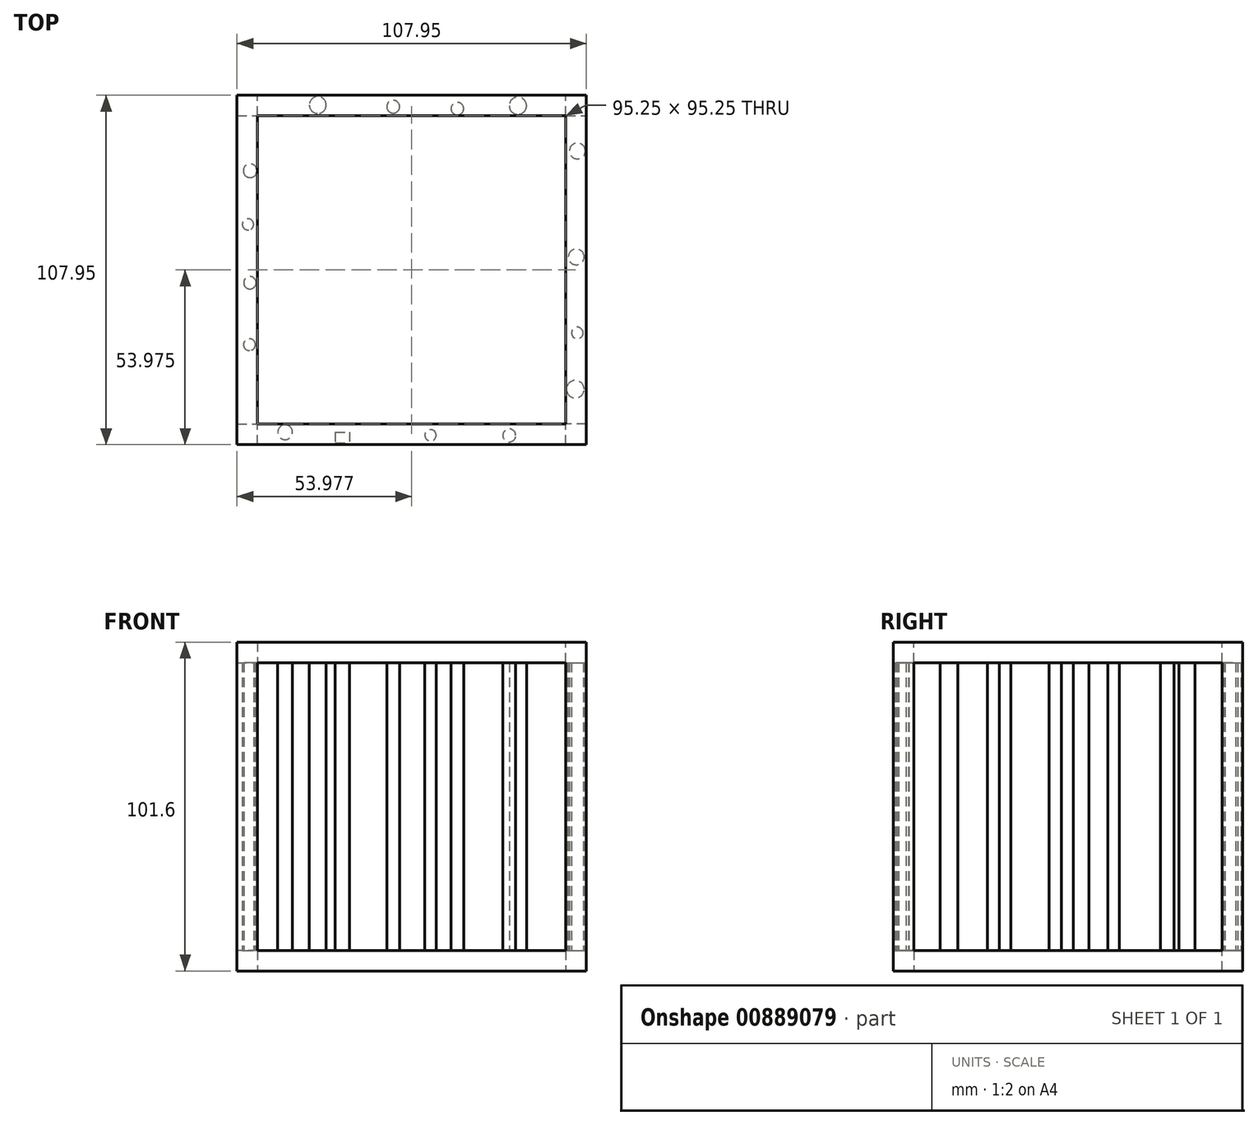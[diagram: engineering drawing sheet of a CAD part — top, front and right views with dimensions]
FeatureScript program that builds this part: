
annotation { "Feature Type Name" : "Feature", "Feature Type Description" : "" }
export const myFeature = defineFeature(function(context is Context, id is Id, definition is map)
    precondition{}
    {
        {
            var Q0;
            Q0=qCreatedBy(makeId("Top.planeOp"),FACE);
            var sketch = newSketch(context, id + "F0", { "sketchPlane" : qUnion([Q0])});
            skLineSegment(sketch, "E0.bottom", {"start": v(-52.32, 56.43) * mm, "end": v(-45.97, 56.43) * mm});
            skLineSegment(sketch, "E0.top", {"start": v(-52.32, 50.08) * mm, "end": v(-45.97, 50.08) * mm});
            skLineSegment(sketch, "E0.left", {"start": v(-52.32, 56.43) * mm, "end": v(-52.32, 50.08) * mm});
            skLineSegment(sketch, "E0.right", {"start": v(-45.97, 56.43) * mm, "end": v(-45.97, 50.08) * mm});
            skSolve(sketch);
        }
        {
            var Q0;
            Q0=makeQuery(id+"F0.imprint","IMPRINT",FACE,{"disambiguationData":[TD([[makeQuery(id+"F0.imprint","IMPRINT",EDGE,{"derivedFrom":sQuery(id+"F0.wireOp",EDGE,"E0.bottom")}),-1.0]])]});
            extrude(context, id + "F1", {"entities" : qUnion([Q0]), "depth" : 101.6 * mm, "offsetDistance" : 25.4 * mm});
        }
        {
            var Q0;
            Q0=makeQuery(id+"F1.opExtrude","SWEPT_FACE",FACE,{"disambiguationData":[OSD([sQuery(id+"F0.wireOp",EDGE,"E0.top")])]});
            var sketch = newSketch(context, id + "F2", { "sketchPlane" : qUnion([Q0])});
            skLineSegment(sketch, "E1.bottom", {"start": v(-45.97, 0) * mm, "end": v(-52.32, 0) * mm});
            skLineSegment(sketch, "E1.top", {"start": v(-45.97, 6.35) * mm, "end": v(-52.32, 6.35) * mm});
            skLineSegment(sketch, "E1.left", {"start": v(-45.97, 0) * mm, "end": v(-45.97, 6.35) * mm});
            skLineSegment(sketch, "E1.right", {"start": v(-52.32, 0) * mm, "end": v(-52.32, 6.35) * mm});
            skSolve(sketch);
        }
        {
            var Q0;
            Q0=makeQuery(id+"F2.imprint","IMPRINT",FACE,{"disambiguationData":[TD([[makeQuery(id+"F2.imprint","IMPRINT",EDGE,{"derivedFrom":sQuery(id+"F2.wireOp",EDGE,"E1.bottom")}),1.0]])]});
            extrude(context, id + "F3", {"entities" : qUnion([Q0]), "operationType" : NewBodyOperationType.ADD, "depth" : 101.6 * mm, "offsetDistance" : 25.4 * mm});
        }
        {
            var Q0;
            Q0=makeQuery(id+"F3.opExtrude","SWEPT_FACE",FACE,{"disambiguationData":[OSD([sQuery(id+"F2.wireOp",EDGE,"E1.top")])]});
            var sketch = newSketch(context, id + "F4", { "sketchPlane" : qUnion([Q0])});
            skLineSegment(sketch, "E2.bottom", {"start": v(-52.32, -51.52) * mm, "end": v(-45.97, -51.52) * mm});
            skLineSegment(sketch, "E2.top", {"start": v(-52.32, -45.17) * mm, "end": v(-45.97, -45.17) * mm});
            skLineSegment(sketch, "E2.left", {"start": v(-52.32, -51.52) * mm, "end": v(-52.32, -45.17) * mm});
            skLineSegment(sketch, "E2.right", {"start": v(-45.97, -51.52) * mm, "end": v(-45.97, -45.17) * mm});
            skSolve(sketch);
        }
        {
            var Q0;
            Q0=makeQuery(id+"F4.imprint","IMPRINT",FACE,{"disambiguationData":[TD([[makeQuery(id+"F4.imprint","IMPRINT",EDGE,{"derivedFrom":sQuery(id+"F4.wireOp",EDGE,"E2.bottom")}),-1.0]])]});
            extrude(context, id + "F5", {"entities" : qUnion([Q0]), "operationType" : NewBodyOperationType.ADD, "depth" : 95.25 * mm, "offsetDistance" : 25.4 * mm});
        }
        {
            var Q0;
            Q0=makeQuery(id+"F1.opExtrude","SWEPT_FACE",FACE,{"disambiguationData":[OSD([sQuery(id+"F0.wireOp",EDGE,"E0.top")])]});
            var sketch = newSketch(context, id + "F6", { "sketchPlane" : qUnion([Q0])});
            skLineSegment(sketch, "E3.bottom", {"start": v(-52.32, 101.6) * mm, "end": v(-45.97, 101.6) * mm});
            skLineSegment(sketch, "E3.top", {"start": v(-52.32, 95.25) * mm, "end": v(-45.97, 95.25) * mm});
            skLineSegment(sketch, "E3.left", {"start": v(-52.32, 101.6) * mm, "end": v(-52.32, 95.25) * mm});
            skLineSegment(sketch, "E3.right", {"start": v(-45.97, 101.6) * mm, "end": v(-45.97, 95.25) * mm});
            skSolve(sketch);
        }
        {
            var Q0;
            Q0 = qSketchRegion(id + "F6", true);
            extrude(context, id + "F7", {"entities" : qUnion([Q0]), "operationType" : NewBodyOperationType.ADD, "depth" : 99.82 * mm, "offsetDistance" : 25.4 * mm});
        }
        {
            var Q0;
            Q0=makeQuery(id+"F7.boolean.opBoolean","MERGE",FACE,{"derivedFrom":[makeQuery(id+"F5.boolean.opBoolean","MERGE",FACE,{"derivedFrom":[makeQuery(id+"F3.boolean.opBoolean","MERGE",FACE,{"derivedFrom":[makeQuery(id+"F1.opExtrude","SWEPT_FACE",FACE,{"disambiguationData":[OSD([sQuery(id+"F0.wireOp",EDGE,"E0.right")])]}),makeQuery(id+"F3.opExtrude","SWEPT_FACE",FACE,{"disambiguationData":[OSD([sQuery(id+"F2.wireOp",EDGE,"E1.left")])]})]}),makeQuery(id+"F5.opExtrude","SWEPT_FACE",FACE,{"disambiguationData":[OSD([sQuery(id+"F4.wireOp",EDGE,"E2.right")])]})]}),makeQuery(id+"F7.opExtrude","SWEPT_FACE",FACE,{"disambiguationData":[OSD([sQuery(id+"F6.wireOp",EDGE,"E3.right")])]})]});
            var sketch = newSketch(context, id + "F8", { "sketchPlane" : qUnion([Q0])});
            skLineSegment(sketch, "E4.bottom", {"start": v(56.43, 0) * mm, "end": v(50.08, 0) * mm});
            skLineSegment(sketch, "E4.top", {"start": v(56.43, 6.35) * mm, "end": v(50.08, 6.35) * mm});
            skLineSegment(sketch, "E4.left", {"start": v(56.43, 0) * mm, "end": v(56.43, 6.35) * mm});
            skLineSegment(sketch, "E4.right", {"start": v(50.08, 0) * mm, "end": v(50.08, 6.35) * mm});
            skSolve(sketch);
        }
        {
            var Q0;
            Q0=makeQuery(id+"F8.imprint","IMPRINT",FACE,{"disambiguationData":[TD([[makeQuery(id+"F8.imprint","IMPRINT",EDGE,{"derivedFrom":sQuery(id+"F8.wireOp",EDGE,"E4.bottom")}),-1.0]])]});
            extrude(context, id + "F9", {"entities" : qUnion([Q0]), "operationType" : NewBodyOperationType.ADD, "depth" : 101.6 * mm, "offsetDistance" : 25.4 * mm});
        }
        {
            var Q0;
            Q0=makeQuery(id+"F7.boolean.opBoolean","MERGE",FACE,{"derivedFrom":[makeQuery(id+"F5.boolean.opBoolean","MERGE",FACE,{"derivedFrom":[makeQuery(id+"F3.boolean.opBoolean","MERGE",FACE,{"derivedFrom":[makeQuery(id+"F1.opExtrude","SWEPT_FACE",FACE,{"disambiguationData":[OSD([sQuery(id+"F0.wireOp",EDGE,"E0.right")])]}),makeQuery(id+"F3.opExtrude","SWEPT_FACE",FACE,{"disambiguationData":[OSD([sQuery(id+"F2.wireOp",EDGE,"E1.left")])]})]}),makeQuery(id+"F5.opExtrude","SWEPT_FACE",FACE,{"disambiguationData":[OSD([sQuery(id+"F4.wireOp",EDGE,"E2.right")])]})]}),makeQuery(id+"F7.opExtrude","SWEPT_FACE",FACE,{"disambiguationData":[OSD([sQuery(id+"F6.wireOp",EDGE,"E3.right")])]})]});
            var sketch = newSketch(context, id + "F10", { "sketchPlane" : qUnion([Q0])});
            skLineSegment(sketch, "E5.bottom", {"start": v(-45.17, 6.35) * mm, "end": v(-51.52, 6.35) * mm});
            skLineSegment(sketch, "E5.top", {"start": v(-45.17, 0) * mm, "end": v(-51.52, 0) * mm});
            skLineSegment(sketch, "E5.left", {"start": v(-45.17, 6.35) * mm, "end": v(-45.17, 0) * mm});
            skLineSegment(sketch, "E5.right", {"start": v(-51.52, 6.35) * mm, "end": v(-51.52, 0) * mm});
            skSolve(sketch);
        }
        {
            var Q0;
            Q0 = qSketchRegion(id + "F10", true);
            var Q1;
            Q1=makeQuery(id+"F10.imprint","IMPRINT",FACE,{"disambiguationData":[TD([[makeQuery(id+"F10.imprint","IMPRINT",EDGE,{"derivedFrom":sQuery(id+"F10.wireOp",EDGE,"E5.bottom")}),1.0]])]});
            extrude(context, id + "F11", {"entities" : qUnion([Q0, Q1]), "operationType" : NewBodyOperationType.ADD, "depth" : 101.6 * mm, "offsetDistance" : 25.4 * mm});
        }
        {
            var Q0;
            Q0=makeQuery(id+"F9.opExtrude","SWEPT_FACE",FACE,{"disambiguationData":[OSD([sQuery(id+"F8.wireOp",EDGE,"E4.right")])]});
            var sketch = newSketch(context, id + "F12", { "sketchPlane" : qUnion([Q0])});
            skLineSegment(sketch, "E6.bottom", {"start": v(55.63, 6.35) * mm, "end": v(49.28, 6.35) * mm});
            skLineSegment(sketch, "E6.top", {"start": v(55.63, 0) * mm, "end": v(49.28, 0) * mm});
            skLineSegment(sketch, "E6.left", {"start": v(55.63, 6.35) * mm, "end": v(55.63, 0) * mm});
            skLineSegment(sketch, "E6.right", {"start": v(49.28, 6.35) * mm, "end": v(49.28, 0) * mm});
            skSolve(sketch);
        }
        {
            var Q0;
            Q0=makeQuery(id+"F12.imprint","IMPRINT",FACE,{"disambiguationData":[TD([[makeQuery(id+"F12.imprint","IMPRINT",EDGE,{"derivedFrom":sQuery(id+"F12.wireOp",EDGE,"E6.bottom")}),1.0]])]});
            extrude(context, id + "F13", {"entities" : qUnion([Q0]), "operationType" : NewBodyOperationType.ADD, "depth" : 97.54 * mm, "offsetDistance" : 25.4 * mm});
        }
        {
            var Q0;
            Q0=makeQuery(id+"F13.boolean.opBoolean","MERGE",FACE,{"derivedFrom":[makeQuery(id+"F9.opExtrude","SWEPT_FACE",FACE,{"disambiguationData":[OSD([sQuery(id+"F8.wireOp",EDGE,"E4.top")])]}),makeQuery(id+"F11.opExtrude","SWEPT_FACE",FACE,{"disambiguationData":[OSD([sQuery(id+"F10.wireOp",EDGE,"E5.bottom")])]}),makeQuery(id+"F13.opExtrude","SWEPT_FACE",FACE,{"disambiguationData":[OSD([sQuery(id+"F12.wireOp",EDGE,"E6.bottom")])]})]});
            var sketch = newSketch(context, id + "F14", { "sketchPlane" : qUnion([Q0])});
            skLineSegment(sketch, "E7.bottom", {"start": v(55.63, -51.52) * mm, "end": v(49.28, -51.52) * mm});
            skLineSegment(sketch, "E7.top", {"start": v(55.63, -45.17) * mm, "end": v(49.28, -45.17) * mm});
            skLineSegment(sketch, "E7.left", {"start": v(55.63, -51.52) * mm, "end": v(55.63, -45.17) * mm});
            skLineSegment(sketch, "E7.right", {"start": v(49.28, -51.52) * mm, "end": v(49.28, -45.17) * mm});
            skSolve(sketch);
        }
        {
            var Q0;
            Q0=makeQuery(id+"F14.imprint","IMPRINT",FACE,{"disambiguationData":[TD([[makeQuery(id+"F14.imprint","IMPRINT",EDGE,{"derivedFrom":sQuery(id+"F14.wireOp",EDGE,"E7.bottom")}),-1.0]])]});
            extrude(context, id + "F15", {"entities" : qUnion([Q0]), "operationType" : NewBodyOperationType.ADD, "depth" : 95.25 * mm, "offsetDistance" : 25.4 * mm});
        }
        {
            var Q0;
            Q0=makeQuery(id+"F15.opExtrude","SWEPT_FACE",FACE,{"disambiguationData":[OSD([sQuery(id+"F14.wireOp",EDGE,"E7.right")])]});
            var sketch = newSketch(context, id + "F16", { "sketchPlane" : qUnion([Q0])});
            skLineSegment(sketch, "E8.bottom", {"start": v(51.52, 101.6) * mm, "end": v(45.17, 101.6) * mm});
            skLineSegment(sketch, "E8.top", {"start": v(51.52, 95.25) * mm, "end": v(45.17, 95.25) * mm});
            skLineSegment(sketch, "E8.left", {"start": v(51.52, 101.6) * mm, "end": v(51.52, 95.25) * mm});
            skLineSegment(sketch, "E8.right", {"start": v(45.17, 101.6) * mm, "end": v(45.17, 95.25) * mm});
            skSolve(sketch);
        }
        {
            var Q0;
            Q0=makeQuery(id+"F16.imprint","IMPRINT",FACE,{"disambiguationData":[TD([[makeQuery(id+"F16.imprint","IMPRINT",EDGE,{"derivedFrom":sQuery(id+"F16.wireOp",EDGE,"E8.bottom")}),1.0]])]});
            extrude(context, id + "F17", {"entities" : qUnion([Q0]), "operationType" : NewBodyOperationType.ADD, "depth" : 96.52 * mm, "offsetDistance" : 25.4 * mm});
        }
        {
            var Q0;
            {var subQ2=sQuery(id+"F4.wireOp",EDGE,"E2.right");var subQ8=makeQuery(id+"F5.opExtrude","SWEPT_FACE",FACE,{"disambiguationData":[OSD([subQ2])]});var subQ9=sQuery(id+"F0.wireOp",EDGE,"E0.bottom");var subQ10=makeQuery(id+"F1.opExtrude","SWEPT_FACE",FACE,{"disambiguationData":[OSD([subQ9])]});var subQ12=sQuery(id+"F2.wireOp",EDGE,"E1.left");var subQ13=makeQuery(id+"F3.opExtrude","SWEPT_FACE",FACE,{"disambiguationData":[OSD([subQ12])]});var subQ14=sQuery(id+"F0.wireOp",EDGE,"E0.right");var subQ15=makeQuery(id+"F1.opExtrude","SWEPT_FACE",FACE,{"disambiguationData":[OSD([subQ14])]});var subQ22=makeQuery(id+"F7.opExtrude","SWEPT_FACE",FACE,{"disambiguationData":[OSD([sQuery(id+"F6.wireOp",EDGE,"E3.right")])]});Q0=makeQuery(id+"F17.boolean.opBoolean","SPLIT",FACE,{"disambiguationData":[TD([subQ10])],"derivedFrom":makeQuery(id+"F11.boolean.opBoolean","SPLIT",FACE,{"disambiguationData":[TD([subQ10])],"derivedFrom":makeQuery(id+"F7.boolean.opBoolean","MERGE",FACE,{"derivedFrom":[makeQuery(id+"F5.boolean.opBoolean","MERGE",FACE,{"derivedFrom":[makeQuery(id+"F3.boolean.opBoolean","MERGE",FACE,{"derivedFrom":[subQ15,subQ13]}),subQ8]}),subQ22]})})});}
            var sketch = newSketch(context, id + "F18", { "sketchPlane" : qUnion([Q0])});
            skLineSegment(sketch, "E9.bottom", {"start": v(50.08, 95.25) * mm, "end": v(56.43, 95.25) * mm});
            skLineSegment(sketch, "E9.top", {"start": v(50.08, 101.6) * mm, "end": v(56.43, 101.6) * mm});
            skLineSegment(sketch, "E9.left", {"start": v(50.08, 95.25) * mm, "end": v(50.08, 101.6) * mm});
            skLineSegment(sketch, "E9.right", {"start": v(56.43, 95.25) * mm, "end": v(56.43, 101.6) * mm});
            skSolve(sketch);
        }
        {
            var Q0;
            Q0=makeQuery(id+"F18.imprint","IMPRINT",FACE,{"disambiguationData":[TD([[makeQuery(id+"F18.imprint","IMPRINT",EDGE,{"derivedFrom":sQuery(id+"F18.wireOp",EDGE,"E9.bottom")}),1.0]])]});
            extrude(context, id + "F19", {"entities" : qUnion([Q0]), "operationType" : NewBodyOperationType.ADD, "depth" : 101.6 * mm, "offsetDistance" : 25.4 * mm});
        }
        {
            var Q0;
            Q0=makeQuery(id+"F19.opExtrude","SWEPT_FACE",FACE,{"disambiguationData":[OSD([sQuery(id+"F18.wireOp",EDGE,"E9.bottom")])]});
            var sketch = newSketch(context, id + "F20", { "sketchPlane" : qUnion([Q0])});
            skLineSegment(sketch, "E10.bottom", {"start": v(55.63, -50.08) * mm, "end": v(49.28, -50.08) * mm});
            skLineSegment(sketch, "E10.top", {"start": v(55.63, -56.43) * mm, "end": v(49.28, -56.43) * mm});
            skLineSegment(sketch, "E10.left", {"start": v(55.63, -50.08) * mm, "end": v(55.63, -56.43) * mm});
            skLineSegment(sketch, "E10.right", {"start": v(49.28, -50.08) * mm, "end": v(49.28, -56.43) * mm});
            skSolve(sketch);
        }
        {
            var Q0;
            Q0=makeQuery(id+"F20.imprint","IMPRINT",FACE,{"disambiguationData":[TD([[makeQuery(id+"F20.imprint","IMPRINT",EDGE,{"derivedFrom":sQuery(id+"F20.wireOp",EDGE,"E10.bottom")}),1.0]])]});
            extrude(context, id + "F21", {"entities" : qUnion([Q0]), "operationType" : NewBodyOperationType.ADD, "depth" : 92.2 * mm, "offsetDistance" : 25.4 * mm});
        }
        {
            var Q0;
            Q0=makeQuery(id+"F17.boolean.opBoolean","MERGE",FACE,{"derivedFrom":[makeQuery(id+"F15.opExtrude","SWEPT_FACE",FACE,{"disambiguationData":[OSD([sQuery(id+"F14.wireOp",EDGE,"E7.top")])]}),makeQuery(id+"F17.opExtrude","SWEPT_FACE",FACE,{"disambiguationData":[OSD([sQuery(id+"F16.wireOp",EDGE,"E8.right")])]})]});
            var sketch = newSketch(context, id + "F22", { "sketchPlane" : qUnion([Q0])});
            skLineSegment(sketch, "E11.bottom", {"start": v(-49.28, 95.25) * mm, "end": v(-55.63, 95.25) * mm});
            skLineSegment(sketch, "E11.top", {"start": v(-49.28, 101.6) * mm, "end": v(-55.63, 101.6) * mm});
            skLineSegment(sketch, "E11.left", {"start": v(-49.28, 95.25) * mm, "end": v(-49.28, 101.6) * mm});
            skLineSegment(sketch, "E11.right", {"start": v(-55.63, 95.25) * mm, "end": v(-55.63, 101.6) * mm});
            skSolve(sketch);
        }
        {
            var Q0;
            Q0 = qSketchRegion(id + "F22", true);
            extrude(context, id + "F23", {"entities" : qUnion([Q0]), "operationType" : NewBodyOperationType.ADD, "depth" : 97.28 * mm, "offsetDistance" : 25.4 * mm});
        }
        {
            var Q0;
            Q0=makeQuery(id+"F3.opExtrude","SWEPT_FACE",FACE,{"disambiguationData":[OSD([sQuery(id+"F2.wireOp",EDGE,"E1.top")])]});
            var sketch = newSketch(context, id + "F24", { "sketchPlane" : qUnion([Q0])});
            skCircle(sketch, "E12", {"center": v(-48.3, 33.1) * mm, "radius": 2.1 * mm});
            skSolve(sketch);
        }
        {
            var Q0;
            {var subQ1=makeQuery(id+"F13.opExtrude","SWEPT_FACE",FACE,{"disambiguationData":[OSD([sQuery(id+"F12.wireOp",EDGE,"E6.bottom")])]});var subQ2=sQuery(id+"F8.wireOp",EDGE,"E4.top");var subQ3=makeQuery(id+"F9.opExtrude","SWEPT_FACE",FACE,{"disambiguationData":[OSD([subQ2])]});var subQ4=sQuery(id+"F10.wireOp",EDGE,"E5.left");var subQ5=makeQuery(id+"F11.opExtrude","SWEPT_FACE",FACE,{"disambiguationData":[OSD([subQ4])]});var subQ7=sQuery(id+"F10.wireOp",EDGE,"E5.bottom");var subQ14=makeQuery(id+"F11.opExtrude","SWEPT_FACE",FACE,{"disambiguationData":[OSD([subQ7])]});Q0=makeQuery(id+"F21.boolean.opBoolean","SPLIT",FACE,{"disambiguationData":[TD([subQ5])],"derivedFrom":makeQuery(id+"F15.boolean.opBoolean","SPLIT",FACE,{"disambiguationData":[TD([makeQuery(id+"F1.opExtrude","SWEPT_FACE",FACE,{"disambiguationData":[OSD([sQuery(id+"F0.wireOp",EDGE,"E0.bottom")])]})])],"derivedFrom":makeQuery(id+"F13.boolean.opBoolean","MERGE",FACE,{"derivedFrom":[subQ3,subQ14,subQ1]})})});}
            var sketch = newSketch(context, id + "F25", { "sketchPlane" : qUnion([Q0])});
            skCircle(sketch, "E13", {"center": v(52.84, 39.23) * mm, "radius": 2.46 * mm});
            skSolve(sketch);
        }
        {
            var Q0;
            Q0=makeQuery(id+"F25.imprint","IMPRINT",FACE,{"disambiguationData":[TD([[makeQuery(id+"F25.imprint","IMPRINT",EDGE,{"derivedFrom":sQuery(id+"F25.wireOp",EDGE,"E13")}),-1.0]])]});
            var sketch = newSketch(context, id + "F26", { "sketchPlane" : qUnion([Q0])});
            skCircle(sketch, "E14", {"center": v(52.49, 6.48) * mm, "radius": 2.45 * mm});
            skSolve(sketch);
        }
        {
            var Q0;
            Q0=makeQuery(id+"F26.imprint","IMPRINT",FACE,{"disambiguationData":[TD([[makeQuery(id+"F26.imprint","IMPRINT",EDGE,{"derivedFrom":sQuery(id+"F26.wireOp",EDGE,"E14")}),-1.0]])]});
            var sketch = newSketch(context, id + "F27", { "sketchPlane" : qUnion([Q0])});
            skCircle(sketch, "E15", {"center": v(52.83, -17) * mm, "radius": 1.8 * mm});
            skSolve(sketch);
        }
        {
            var Q0;
            Q0=makeQuery(id+"F25.imprint","IMPRINT",FACE,{"disambiguationData":[TD([[makeQuery(id+"F25.imprint","IMPRINT",EDGE,{"derivedFrom":sQuery(id+"F25.wireOp",EDGE,"E13")}),1.0]])]});
            extrude(context, id + "F28", {"entities" : qUnion([Q0]), "operationType" : NewBodyOperationType.ADD, "depth" : 89.92 * mm, "offsetDistance" : 25.4 * mm});
        }
        {
            var Q0;
            Q0=makeQuery(id+"F26.imprint","IMPRINT",FACE,{"disambiguationData":[TD([[makeQuery(id+"F26.imprint","IMPRINT",EDGE,{"derivedFrom":sQuery(id+"F26.wireOp",EDGE,"E14")}),1.0]])]});
            extrude(context, id + "F29", {"entities" : qUnion([Q0]), "operationType" : NewBodyOperationType.ADD, "depth" : 91.19 * mm, "offsetDistance" : 25.4 * mm});
        }
        {
            var Q0;
            Q0=makeQuery(id+"F27.imprint","IMPRINT",FACE,{"disambiguationData":[TD([[makeQuery(id+"F27.imprint","IMPRINT",EDGE,{"derivedFrom":sQuery(id+"F27.wireOp",EDGE,"E15")}),-1.0]])]});
            var sketch = newSketch(context, id + "F30", { "sketchPlane" : qUnion([Q0])});
            skCircle(sketch, "E16", {"center": v(52.2, -34.4) * mm, "radius": 2.72 * mm});
            skSolve(sketch);
        }
        {
            var Q0;
            Q0 = qSketchRegion(id + "F30", true);
            extrude(context, id + "F31", {"entities" : qUnion([Q0]), "operationType" : NewBodyOperationType.ADD, "depth" : 91.19 * mm, "offsetDistance" : 25.4 * mm});
        }
        {
            var Q0;
            Q0=makeQuery(id+"F27.imprint","IMPRINT",FACE,{"disambiguationData":[TD([[makeQuery(id+"F27.imprint","IMPRINT",EDGE,{"derivedFrom":sQuery(id+"F27.wireOp",EDGE,"E15")}),1.0]])]});
            extrude(context, id + "F32", {"entities" : qUnion([Q0]), "operationType" : NewBodyOperationType.ADD, "depth" : 92.46 * mm, "offsetDistance" : 25.4 * mm});
        }
        {
            var Q0;
            {var subQ0=makeQuery(id+"F11.opExtrude","SWEPT_FACE",FACE,{"disambiguationData":[OSD([sQuery(id+"F10.wireOp",EDGE,"E5.bottom")])]});var subQ1=makeQuery(id+"F9.opExtrude","SWEPT_FACE",FACE,{"disambiguationData":[OSD([sQuery(id+"F8.wireOp",EDGE,"E4.top")])]});var subQ2=makeQuery(id+"F13.opExtrude","SWEPT_FACE",FACE,{"disambiguationData":[OSD([sQuery(id+"F12.wireOp",EDGE,"E6.bottom")])]});Q0=makeQuery(id+"F15.boolean.opBoolean","SPLIT",FACE,{"disambiguationData":[TD([makeQuery(id+"F5.opExtrude","SWEPT_FACE",FACE,{"disambiguationData":[OSD([sQuery(id+"F4.wireOp",EDGE,"E2.bottom")])]})])],"derivedFrom":makeQuery(id+"F13.boolean.opBoolean","MERGE",FACE,{"derivedFrom":[subQ1,subQ0,subQ2]})});}
            var sketch = newSketch(context, id + "F33", { "sketchPlane" : qUnion([Q0])});
            skCircle(sketch, "E17", {"center": v(31.78, -48.68) * mm, "radius": 2 * mm});
            skSolve(sketch);
        }
        {
            var Q0;
            Q0=makeQuery(id+"F33.imprint","IMPRINT",FACE,{"disambiguationData":[TD([[makeQuery(id+"F33.imprint","IMPRINT",EDGE,{"derivedFrom":sQuery(id+"F33.wireOp",EDGE,"E17")}),-1.0]])]});
            var sketch = newSketch(context, id + "F34", { "sketchPlane" : qUnion([Q0])});
            skCircle(sketch, "E18", {"center": v(7.44, -48.59) * mm, "radius": 1.74 * mm});
            skSolve(sketch);
        }
        {
            var Q0;
            Q0=makeQuery(id+"F33.imprint","IMPRINT",FACE,{"disambiguationData":[TD([[makeQuery(id+"F33.imprint","IMPRINT",EDGE,{"derivedFrom":sQuery(id+"F33.wireOp",EDGE,"E17")}),-1.0]])]});
            var sketch = newSketch(context, id + "F35", { "sketchPlane" : qUnion([Q0])});
            skLineSegment(sketch, "E19.bottom", {"start": v(-21.99, -47.62) * mm, "end": v(-17.64, -47.62) * mm});
            skLineSegment(sketch, "E19.top", {"start": v(-21.99, -51.02) * mm, "end": v(-17.64, -51.02) * mm});
            skLineSegment(sketch, "E19.left", {"start": v(-21.99, -47.62) * mm, "end": v(-21.99, -51.02) * mm});
            skLineSegment(sketch, "E19.right", {"start": v(-17.64, -47.62) * mm, "end": v(-17.64, -51.02) * mm});
            skSolve(sketch);
        }
        {
            var Q0;
            Q0=makeQuery(id+"F34.imprint","IMPRINT",FACE,{"disambiguationData":[TD([[makeQuery(id+"F34.imprint","IMPRINT",EDGE,{"derivedFrom":sQuery(id+"F34.wireOp",EDGE,"E18")}),-1.0]])]});
            var sketch = newSketch(context, id + "F36", { "sketchPlane" : qUnion([Q0])});
            skCircle(sketch, "E20", {"center": v(-37.47, -47.68) * mm, "radius": 2.28 * mm});
            skSolve(sketch);
        }
        {
            var Q0;
            Q0=makeQuery(id+"F36.imprint","IMPRINT",FACE,{"disambiguationData":[TD([[makeQuery(id+"F36.imprint","IMPRINT",EDGE,{"derivedFrom":sQuery(id+"F36.wireOp",EDGE,"E20")}),1.0]])]});
            var Q1;
            Q1=makeQuery(id+"F35.imprint","IMPRINT",FACE,{"disambiguationData":[TD([[makeQuery(id+"F35.imprint","IMPRINT",EDGE,{"derivedFrom":sQuery(id+"F35.wireOp",EDGE,"E19.bottom")}),-1.0]])]});
            var Q2;
            Q2=makeQuery(id+"F33.imprint","IMPRINT",FACE,{"disambiguationData":[TD([[makeQuery(id+"F33.imprint","IMPRINT",EDGE,{"derivedFrom":sQuery(id+"F33.wireOp",EDGE,"E17")}),1.0]])]});
            var Q3;
            Q3=makeQuery(id+"F34.imprint","IMPRINT",FACE,{"disambiguationData":[TD([[makeQuery(id+"F34.imprint","IMPRINT",EDGE,{"derivedFrom":sQuery(id+"F34.wireOp",EDGE,"E18")}),1.0]])]});
            extrude(context, id + "F37", {"entities" : qUnion([Q0, Q1, Q2, Q3]), "operationType" : NewBodyOperationType.ADD, "depth" : 95.25 * mm, "offsetDistance" : 25.4 * mm});
        }
        {
            var Q0;
            Q0=makeQuery(id+"F24.imprint","IMPRINT",FACE,{"disambiguationData":[TD([[makeQuery(id+"F24.imprint","IMPRINT",EDGE,{"derivedFrom":sQuery(id+"F24.wireOp",EDGE,"E12")}),-1.0]])]});
            var sketch = newSketch(context, id + "F38", { "sketchPlane" : qUnion([Q0])});
            skCircle(sketch, "E21", {"center": v(-48.95, 16.54) * mm, "radius": 1.74 * mm});
            skSolve(sketch);
        }
        {
            var Q0;
            Q0=makeQuery(id+"F38.imprint","IMPRINT",FACE,{"disambiguationData":[TD([[makeQuery(id+"F38.imprint","IMPRINT",EDGE,{"derivedFrom":sQuery(id+"F38.wireOp",EDGE,"E21")}),-1.0]])]});
            var sketch = newSketch(context, id + "F39", { "sketchPlane" : qUnion([Q0])});
            skCircle(sketch, "E22", {"center": v(-48.34, -1.5) * mm, "radius": 1.92 * mm});
            skCircle(sketch, "E23", {"center": v(-48.5, -20.61) * mm, "radius": 1.83 * mm});
            skSolve(sketch);
        }
        {
            var Q0;
            Q0=makeQuery(id+"F24.imprint","IMPRINT",FACE,{"disambiguationData":[TD([[makeQuery(id+"F24.imprint","IMPRINT",EDGE,{"derivedFrom":sQuery(id+"F24.wireOp",EDGE,"E12")}),1.0]])]});
            var Q1;
            Q1=makeQuery(id+"F38.imprint","IMPRINT",FACE,{"disambiguationData":[TD([[makeQuery(id+"F38.imprint","IMPRINT",EDGE,{"derivedFrom":sQuery(id+"F38.wireOp",EDGE,"E21")}),1.0]])]});
            var Q2;
            Q2=makeQuery(id+"F39.imprint","IMPRINT",FACE,{"disambiguationData":[TD([[makeQuery(id+"F39.imprint","IMPRINT",EDGE,{"derivedFrom":sQuery(id+"F39.wireOp",EDGE,"E22")}),1.0]])]});
            var Q3;
            Q3=makeQuery(id+"F39.imprint","IMPRINT",FACE,{"disambiguationData":[TD([[makeQuery(id+"F39.imprint","IMPRINT",EDGE,{"derivedFrom":sQuery(id+"F39.wireOp",EDGE,"E23")}),1.0]])]});
            extrude(context, id + "F40", {"entities" : qUnion([Q0, Q1, Q2, Q3]), "operationType" : NewBodyOperationType.ADD, "depth" : 95.25 * mm, "offsetDistance" : 25.4 * mm});
        }
        {
            var Q0;
            {var subQ4=sQuery(id+"F8.wireOp",EDGE,"E4.top");var subQ5=makeQuery(id+"F9.opExtrude","SWEPT_FACE",FACE,{"disambiguationData":[OSD([subQ4])]});var subQ6=makeQuery(id+"F1.opExtrude","SWEPT_FACE",FACE,{"disambiguationData":[OSD([sQuery(id+"F0.wireOp",EDGE,"E0.bottom")])]});var subQ7=makeQuery(id+"F13.opExtrude","SWEPT_FACE",FACE,{"disambiguationData":[OSD([sQuery(id+"F12.wireOp",EDGE,"E6.bottom")])]});var subQ15=sQuery(id+"F10.wireOp",EDGE,"E5.bottom");var subQ16=makeQuery(id+"F11.opExtrude","SWEPT_FACE",FACE,{"disambiguationData":[OSD([subQ15])]});Q0=makeQuery(id+"F21.boolean.opBoolean","SPLIT",FACE,{"disambiguationData":[TD([subQ6])],"derivedFrom":makeQuery(id+"F15.boolean.opBoolean","SPLIT",FACE,{"disambiguationData":[TD([subQ6])],"derivedFrom":makeQuery(id+"F13.boolean.opBoolean","MERGE",FACE,{"derivedFrom":[subQ5,subQ16,subQ7]})})});}
            var sketch = newSketch(context, id + "F41", { "sketchPlane" : qUnion([Q0])});
            skCircle(sketch, "E24", {"center": v(34.44, 53.19) * mm, "radius": 2.67 * mm});
            skSolve(sketch);
        }
        {
            var Q0;
            Q0=makeQuery(id+"F41.imprint","IMPRINT",FACE,{"disambiguationData":[TD([[makeQuery(id+"F41.imprint","IMPRINT",EDGE,{"derivedFrom":sQuery(id+"F41.wireOp",EDGE,"E24")}),-1.0]])]});
            var sketch = newSketch(context, id + "F42", { "sketchPlane" : qUnion([Q0])});
            skCircle(sketch, "E25", {"center": v(15.75, 52.28) * mm, "radius": 1.95 * mm});
            skSolve(sketch);
        }
        {
            var Q0;
            Q0=makeQuery(id+"F41.imprint","IMPRINT",FACE,{"disambiguationData":[TD([[makeQuery(id+"F41.imprint","IMPRINT",EDGE,{"derivedFrom":sQuery(id+"F41.wireOp",EDGE,"E24")}),-1.0]])]});
            var sketch = newSketch(context, id + "F43", { "sketchPlane" : qUnion([Q0])});
            skCircle(sketch, "E26", {"center": v(-4.06, 52.9) * mm, "radius": 1.99 * mm});
            skCircle(sketch, "E27", {"center": v(-27.37, 53.41) * mm, "radius": 2.6 * mm});
            skSolve(sketch);
        }
        {
            var Q0;
            Q0=makeQuery(id+"F41.imprint","IMPRINT",FACE,{"disambiguationData":[TD([[makeQuery(id+"F41.imprint","IMPRINT",EDGE,{"derivedFrom":sQuery(id+"F41.wireOp",EDGE,"E24")}),1.0]])]});
            var Q1;
            Q1=makeQuery(id+"F42.imprint","IMPRINT",FACE,{"disambiguationData":[TD([[makeQuery(id+"F42.imprint","IMPRINT",EDGE,{"derivedFrom":sQuery(id+"F42.wireOp",EDGE,"E25")}),1.0]])]});
            var Q2;
            Q2=makeQuery(id+"F43.imprint","IMPRINT",FACE,{"disambiguationData":[TD([[makeQuery(id+"F43.imprint","IMPRINT",EDGE,{"derivedFrom":sQuery(id+"F43.wireOp",EDGE,"E27")}),1.0]])]});
            var Q3;
            Q3=makeQuery(id+"F43.imprint","IMPRINT",FACE,{"disambiguationData":[TD([[makeQuery(id+"F43.imprint","IMPRINT",EDGE,{"derivedFrom":sQuery(id+"F43.wireOp",EDGE,"E26")}),1.0]])]});
            extrude(context, id + "F44", {"entities" : qUnion([Q0, Q1, Q2, Q3]), "operationType" : NewBodyOperationType.ADD, "depth" : 95.25 * mm, "offsetDistance" : 25.4 * mm});
        }
    });
